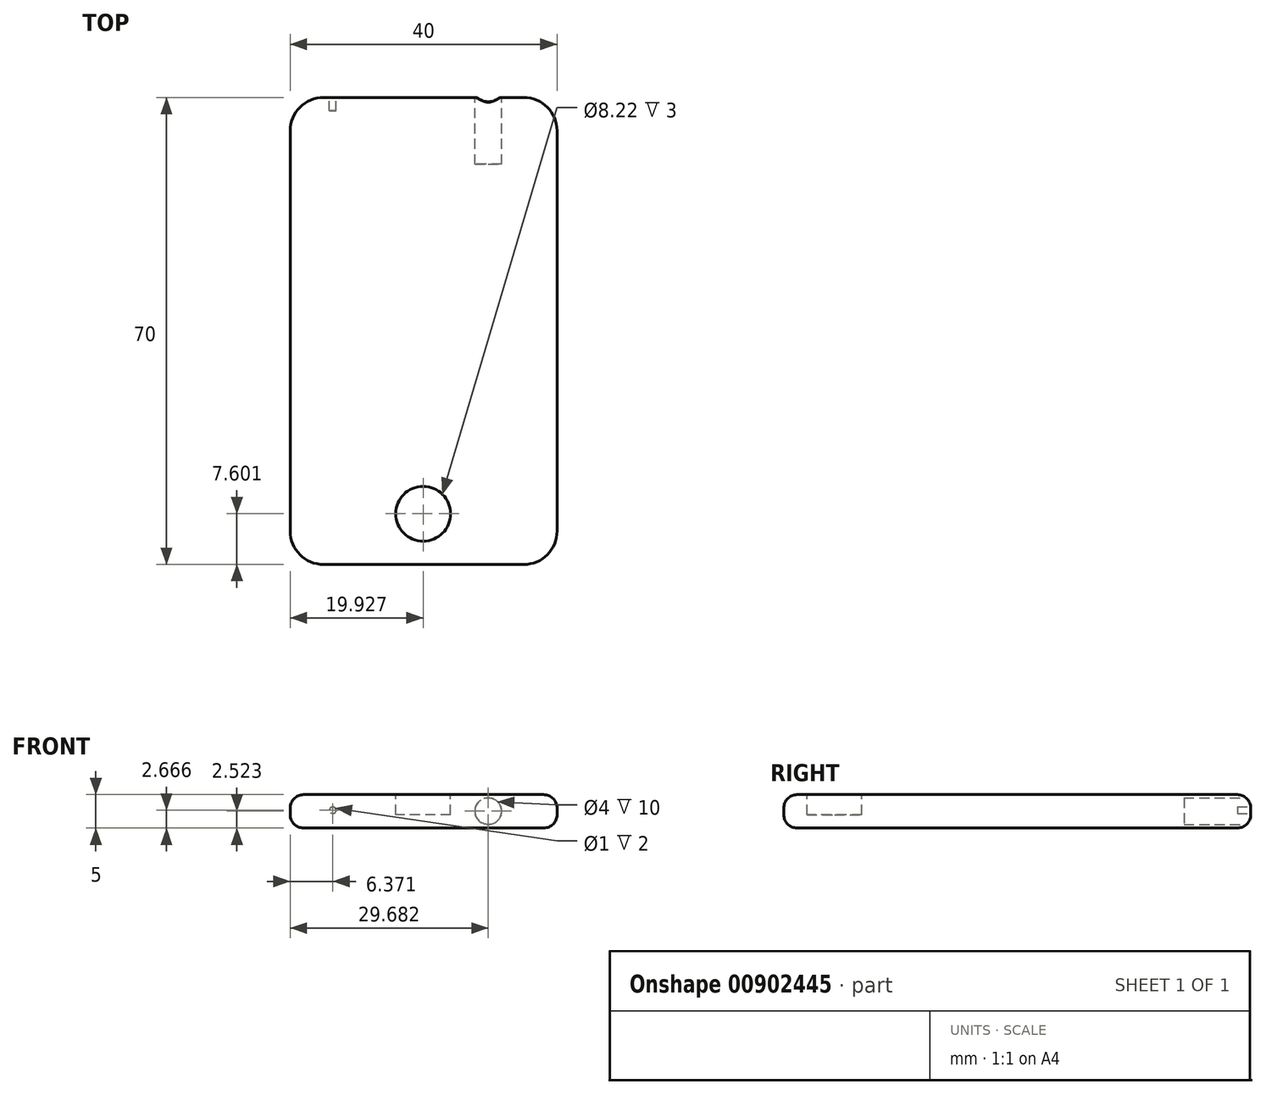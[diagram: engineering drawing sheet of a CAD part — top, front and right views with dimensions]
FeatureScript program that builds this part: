
annotation { "Feature Type Name" : "Feature", "Feature Type Description" : "" }
export const myFeature = defineFeature(function(context is Context, id is Id, definition is map)
    precondition{}
    {
        {
            var Q0;
            Q0=qCreatedBy(makeId("Top.planeOp"),FACE);
            var sketch = newSketch(context, id + "F0", { "sketchPlane" : qUnion([Q0])});
            skLineSegment(sketch, "E0.bottom", {"start": v(0, 0) * mm, "end": v(40, 0) * mm});
            skLineSegment(sketch, "E0.top", {"start": v(0, 70) * mm, "end": v(40, 70) * mm});
            skLineSegment(sketch, "E0.left", {"start": v(0, 0) * mm, "end": v(0, 70) * mm});
            skLineSegment(sketch, "E0.right", {"start": v(40, 0) * mm, "end": v(40, 70) * mm});
            skSolve(sketch);
        }
        {
            var Q0;
            Q0 = qSketchRegion(id + "F0", true);
            extrude(context, id + "F1", {"entities" : qUnion([Q0]), "depth" : 5 * mm, "offsetDistance" : 25 * mm});
        }
        {
            var Q0;
            Q0=makeQuery(id+"F1.opExtrude","SWEPT_EDGE",EDGE,{"disambiguationData":[OSD([sQuery(id+"F0.wireOp",EDGE,"E0.bottom"),sQuery(id+"F0.wireOp",EDGE,"E0.right")])]});
            var Q1;
            Q1=makeQuery(id+"F1.opExtrude","SWEPT_EDGE",EDGE,{"disambiguationData":[OSD([sQuery(id+"F0.wireOp",EDGE,"E0.top"),sQuery(id+"F0.wireOp",EDGE,"E0.right")])]});
            var Q2;
            Q2=makeQuery(id+"F1.opExtrude","SWEPT_EDGE",EDGE,{"disambiguationData":[OSD([sQuery(id+"F0.wireOp",EDGE,"E0.bottom"),sQuery(id+"F0.wireOp",EDGE,"E0.left")])]});
            var Q3;
            Q3=makeQuery(id+"F1.opExtrude","SWEPT_EDGE",EDGE,{"disambiguationData":[OSD([sQuery(id+"F0.wireOp",EDGE,"E0.top"),sQuery(id+"F0.wireOp",EDGE,"E0.left")])]});
            fillet(context, id + "F2", {"entities" : qUnion([Q0, Q1, Q2, Q3]), "radius" : 5 * mm, "tangentPropagation" : true, "allowEdgeOverflow" : false});
        }
        {
            var Q0;
            Q0=makeQuery(id+"F1.opExtrude","SWEPT_FACE",FACE,{"disambiguationData":[OSD([sQuery(id+"F0.wireOp",EDGE,"E0.top")])]});
            var sketch = newSketch(context, id + "F3", { "sketchPlane" : qUnion([Q0])});
            skCircle(sketch, "E1", {"center": v(-29.68, 2.52) * mm, "radius": 2 * mm});
            skSolve(sketch);
        }
        {
            var Q0;
            Q0 = qSketchRegion(id + "F3", true);
            var Q1;
            Q1=sQuery(id+"F3.wireOp",EDGE,"E1");
            extrude(context, id + "F4", {"entities" : qUnion([Q0]), "operationType" : NewBodyOperationType.REMOVE, "surfaceEntities" : qUnion([Q1]), "oppositeDirection" : true, "depth" : 10 * mm, "offsetDistance" : 25 * mm});
        }
        {
            var Q0;
            Q0=makeQuery(id+"F1.opExtrude","CAP_EDGE",EDGE,{"disambiguationData":[OSD([sQuery(id+"F0.wireOp",EDGE,"E0.top")])],"isStart":false});
            var Q1;
            Q1=makeQuery(id+"F1.opExtrude","CAP_EDGE",EDGE,{"disambiguationData":[OSD([sQuery(id+"F0.wireOp",EDGE,"E0.top")])],"isStart":true});
            fillet(context, id + "F5", {"entities" : qUnion([Q0, Q1]), "radius" : 2 * mm, "tangentPropagation" : true, "allowEdgeOverflow" : false});
        }
        {
            var Q0;
            Q0=makeQuery(id+"F1.opExtrude","CAP_FACE",FACE,{"disambiguationData":[OSD([sQuery(id+"F0.wireOp",EDGE,"E0.bottom"),sQuery(id+"F0.wireOp",EDGE,"E0.top"),sQuery(id+"F0.wireOp",EDGE,"E0.left"),sQuery(id+"F0.wireOp",EDGE,"E0.right")])],"isStart":false});
            var sketch = newSketch(context, id + "F6", { "sketchPlane" : qUnion([Q0])});
            skCircle(sketch, "E2", {"center": v(19.93, 7.6) * mm, "radius": 4.1 * mm});
            skSolve(sketch);
        }
        {
            var Q0;
            Q0=makeQuery(id+"F6.imprint","IMPRINT",FACE,{"disambiguationData":[TD([[makeQuery(id+"F6.imprint","IMPRINT",EDGE,{"derivedFrom":sQuery(id+"F6.wireOp",EDGE,"E2")}),1.0]])]});
            extrude(context, id + "F7", {"entities" : qUnion([Q0]), "operationType" : NewBodyOperationType.REMOVE, "oppositeDirection" : true, "depth" : 3 * mm, "offsetDistance" : 25 * mm});
        }
        {
            var Q0;
            Q0=makeQuery(id+"F3.imprint","IMPRINT",FACE,{"disambiguationData":[TD([[makeQuery(id+"F3.imprint","IMPRINT",EDGE,{"derivedFrom":sQuery(id+"F3.wireOp",EDGE,"E1")}),-1.0]])]});
            var sketch = newSketch(context, id + "F8", { "sketchPlane" : qUnion([Q0])});
            skCircle(sketch, "E3", {"center": v(-6.37, 2.67) * mm, "radius": 0.5 * mm});
            skCircle(sketch, "E4", {"center": v(-7.93, 2.7) * mm, "radius": 0.5 * mm});
            skSolve(sketch);
        }
        {
            var Q0;
            Q0=makeQuery(id+"F8.imprint","IMPRINT",FACE,{"disambiguationData":[TD([[makeQuery(id+"F8.imprint","IMPRINT",EDGE,{"derivedFrom":sQuery(id+"F8.wireOp",EDGE,"E3")}),1.0]])]});
            extrude(context, id + "F9", {"entities" : qUnion([Q0]), "operationType" : NewBodyOperationType.REMOVE, "oppositeDirection" : true, "depth" : 2 * mm, "offsetDistance" : 25 * mm});
        }
    });
